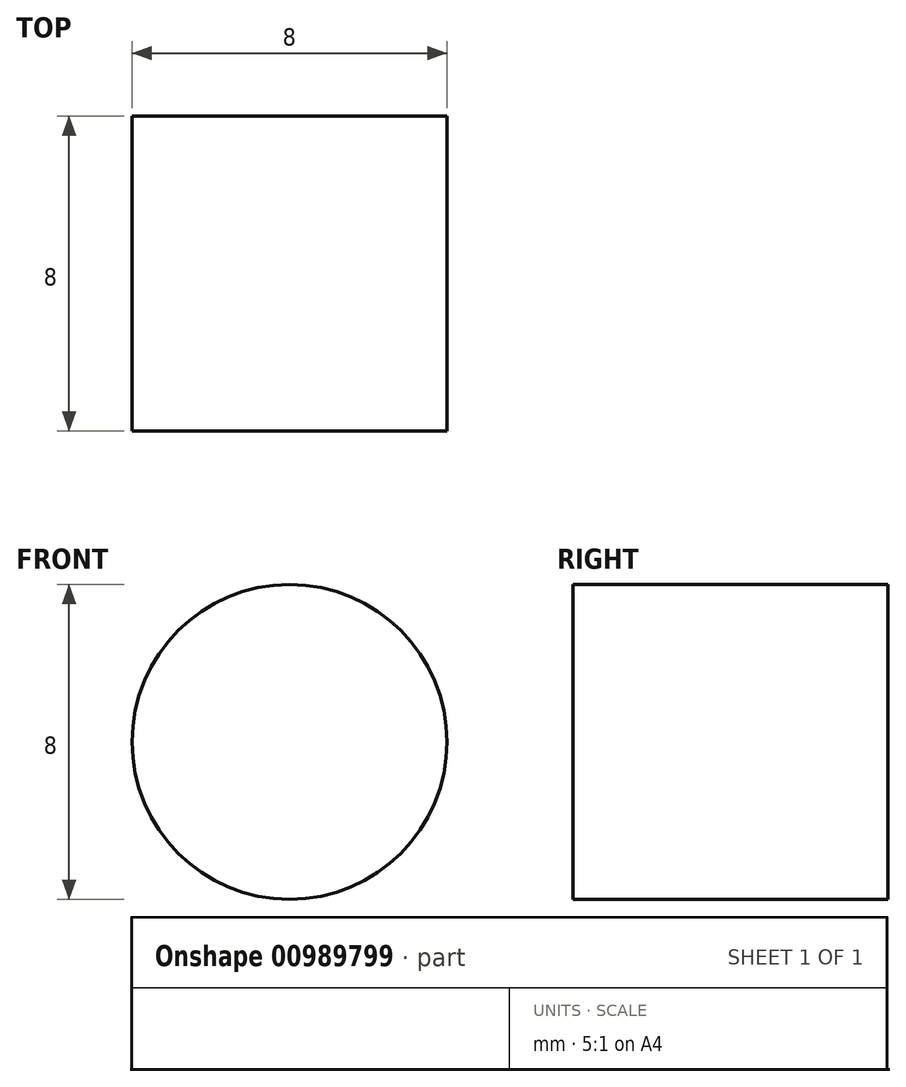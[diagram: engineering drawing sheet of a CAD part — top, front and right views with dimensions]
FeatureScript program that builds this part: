
annotation { "Feature Type Name" : "Feature", "Feature Type Description" : "" }
export const myFeature = defineFeature(function(context is Context, id is Id, definition is map)
    precondition{}
    {
        {
            var Q0;
            Q0=qCreatedBy(makeId("Front.planeOp"),FACE);
            var sketch = newSketch(context, id + "F0", { "sketchPlane" : qUnion([Q0])});
            skCircle(sketch, "E0", {"center": v(0, 0) * mm, "radius": 4 * mm});
            skSolve(sketch);
        }
        {
            var Q0;
            Q0 = qSketchRegion(id + "F0", true);
            extrude(context, id + "F1", {"entities" : qUnion([Q0]), "depth" : 8 * mm, "offsetDistance" : 25 * mm});
        }
    });
